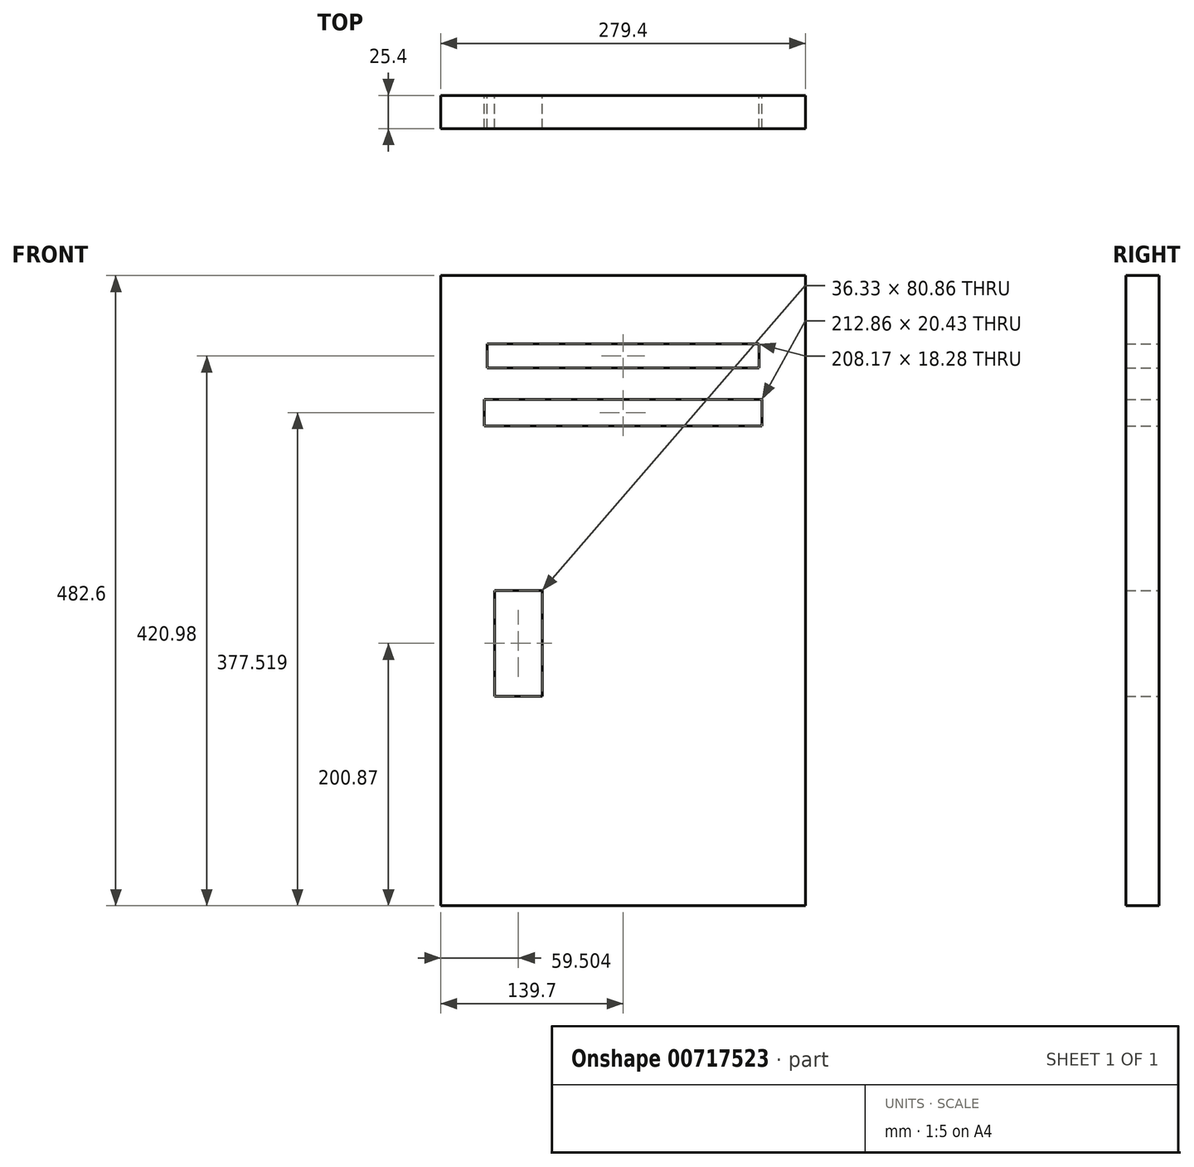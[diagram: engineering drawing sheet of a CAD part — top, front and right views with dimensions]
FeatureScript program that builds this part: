
annotation { "Feature Type Name" : "Feature", "Feature Type Description" : "" }
export const myFeature = defineFeature(function(context is Context, id is Id, definition is map)
    precondition{}
    {
        {
            var Q0;
            Q0=qCreatedBy(makeId("Front.planeOp"),FACE);
            var sketch = newSketch(context, id + "F0", { "sketchPlane" : qUnion([Q0])});
            skLineSegment(sketch, "E0.bottom", {"start": v(139.7, 241.3) * mm, "end": v(-139.7, 241.3) * mm});
            skLineSegment(sketch, "E0.top", {"start": v(139.7, -241.3) * mm, "end": v(-139.7, -241.3) * mm});
            skLineSegment(sketch, "E0.left", {"start": v(139.7, 241.3) * mm, "end": v(139.7, -241.3) * mm});
            skLineSegment(sketch, "E0.right", {"start": v(-139.7, 241.3) * mm, "end": v(-139.7, -241.3) * mm});
            skPoint(sketch, "E0.middle", {"position": v(0, 0) * mm});
            skLineSegment(sketch, "E1.bottom", {"start": v(104.09, 188.82) * mm, "end": v(-104.09, 188.82) * mm});
            skLineSegment(sketch, "E1.top", {"start": v(104.09, 170.54) * mm, "end": v(-104.09, 170.54) * mm});
            skLineSegment(sketch, "E1.left", {"start": v(104.09, 188.82) * mm, "end": v(104.09, 170.54) * mm});
            skLineSegment(sketch, "E1.right", {"start": v(-104.09, 188.82) * mm, "end": v(-104.09, 170.54) * mm});
            skPoint(sketch, "E1.middle", {"position": v(0, 179.68) * mm});
            skLineSegment(sketch, "E2.bottom", {"start": v(106.43, 146.44) * mm, "end": v(-106.43, 146.44) * mm});
            skLineSegment(sketch, "E2.top", {"start": v(106.43, 126) * mm, "end": v(-106.43, 126) * mm});
            skLineSegment(sketch, "E2.left", {"start": v(106.43, 146.44) * mm, "end": v(106.43, 126) * mm});
            skLineSegment(sketch, "E2.right", {"start": v(-106.43, 146.44) * mm, "end": v(-106.43, 126) * mm});
            skPoint(sketch, "E2.middle", {"position": v(0, 136.22) * mm});
            skPoint(sketch, "E3.firstSnap0", {"position": v(-139.7, 0) * mm});
            skLineSegment(sketch, "E3.bottom", {"start": v(-98.36, 0) * mm, "end": v(-62.03, 0) * mm});
            skLineSegment(sketch, "E3.top", {"start": v(-98.36, -80.86) * mm, "end": v(-62.03, -80.86) * mm});
            skLineSegment(sketch, "E3.left", {"start": v(-98.36, 0) * mm, "end": v(-98.36, -80.86) * mm});
            skLineSegment(sketch, "E3.right", {"start": v(-62.03, 0) * mm, "end": v(-62.03, -80.86) * mm});
            skSolve(sketch);
        }
        {
            var Q0;
            Q0=makeQuery(id+"F0.imprint","IMPRINT",FACE,{"disambiguationData":[TD([[makeQuery(id+"F0.imprint","IMPRINT",EDGE,{"derivedFrom":sQuery(id+"F0.wireOp",EDGE,"E0.bottom")}),1.0]])]});
            extrude(context, id + "F1", {"entities" : qUnion([Q0]), "depth" : 25.4 * mm, "offsetDistance" : 25.4 * mm});
        }
    });
